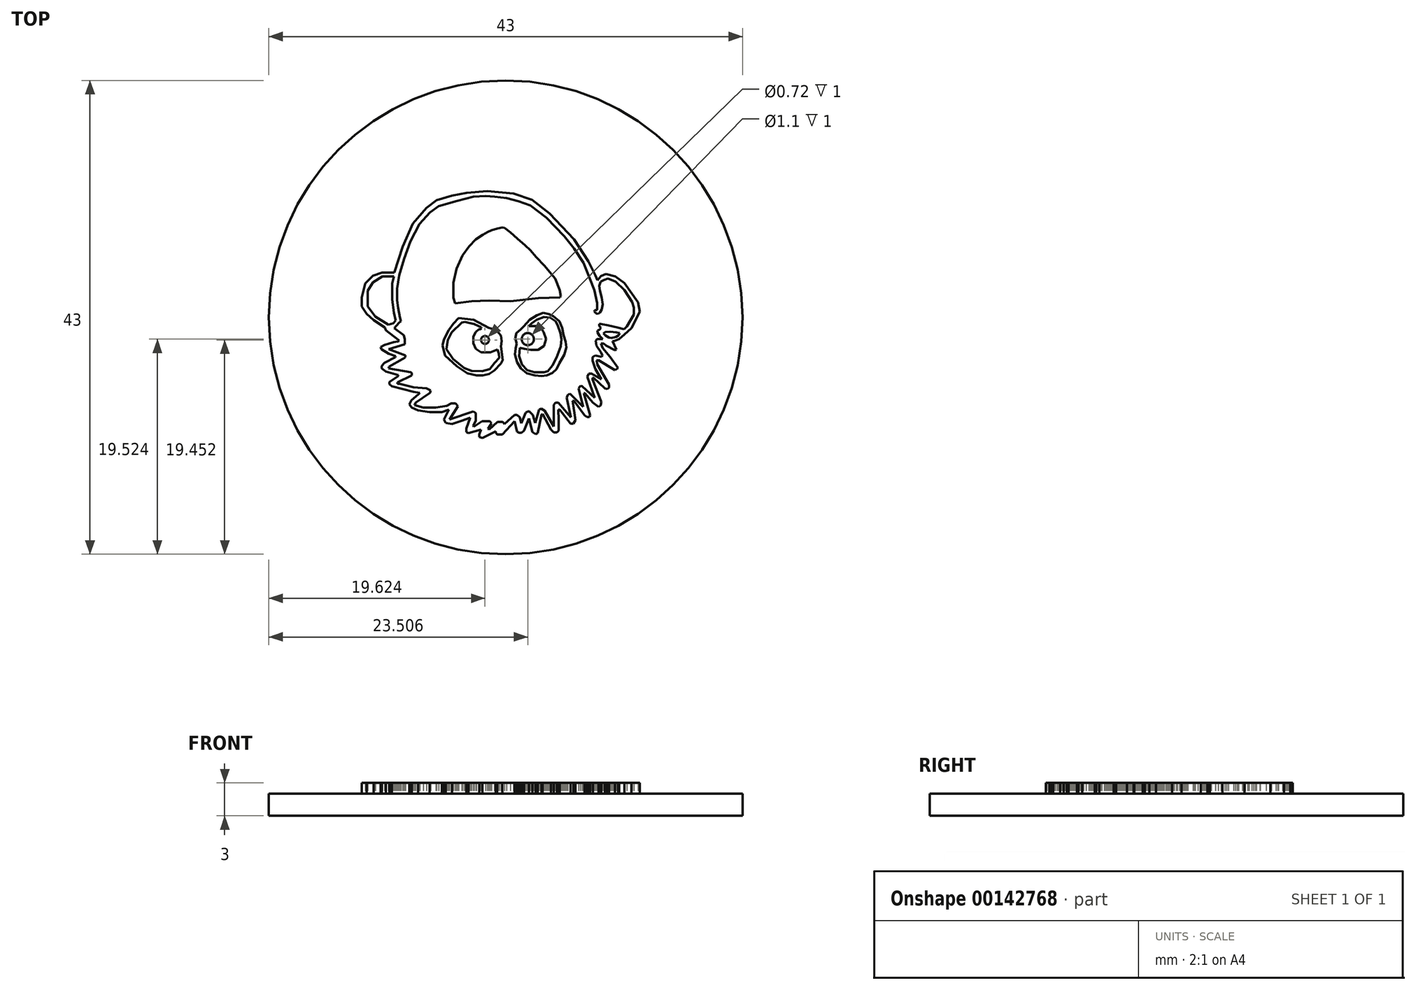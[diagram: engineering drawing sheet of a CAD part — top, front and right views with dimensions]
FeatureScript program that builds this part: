
annotation { "Feature Type Name" : "Feature", "Feature Type Description" : "" }
export const myFeature = defineFeature(function(context is Context, id is Id, definition is map)
    precondition{}
    {
        {
            var Q0;
            Q0=qCreatedBy(makeId("Top.planeOp"),FACE);
            var sketch = newSketch(context, id + "F0", { "sketchPlane" : qUnion([Q0])});
            skLineSegment(sketch, "E0.bottom", {"start": v(22, -30) * mm, "end": v(-22, -30) * mm});
            skLineSegment(sketch, "E0.top", {"start": v(22, 30) * mm, "end": v(-22, 30) * mm});
            skLineSegment(sketch, "E0.left", {"start": v(22, -30) * mm, "end": v(22, 30) * mm});
            skLineSegment(sketch, "E0.right", {"start": v(-22, -30) * mm, "end": v(-22, 30) * mm});
            skPoint(sketch, "E0.middle", {"position": v(0, 0) * mm});
            skCircle(sketch, "E1", {"center": v(0, 0) * mm, "radius": 21.5 * mm, "construction": true});
            skSolve(sketch);
        }
        {
            var Q0;
            Q0=qSketchRegion(id+"F0",true);
            extrude(context, id + "F1", {"entities" : qUnion([Q0]), "oppositeDirection" : true, "depth" : 2 * mm});
        }
        {
            var Q0;
            Q0=makeQuery(id+"F1.opExtrude","CAP_FACE",FACE,{"disambiguationData":[OSD([sQuery(id+"F0.wireOp",EDGE,"E0.bottom"),sQuery(id+"F0.wireOp",EDGE,"E0.top"),sQuery(id+"F0.wireOp",EDGE,"E0.left"),sQuery(id+"F0.wireOp",EDGE,"E0.right")])],"isStart":false});
            var sketch = newSketch(context, id + "F2", { "sketchPlane" : qUnion([Q0])});
            skLineSegment(sketch, "E2", {"start": v(-9.75, 2.02) * mm, "end": v(-10.89, 1.18) * mm});
            skLineSegment(sketch, "E3", {"start": v(-10.89, 1.18) * mm, "end": v(-10.98, 0.9) * mm});
            skLineSegment(sketch, "E4", {"start": v(-10.98, 0.9) * mm, "end": v(-12, 0.26) * mm});
            skLineSegment(sketch, "E5", {"start": v(-12, 0.26) * mm, "end": v(-12.62, -0.33) * mm});
            skLineSegment(sketch, "E6", {"start": v(-12.62, -0.33) * mm, "end": v(-13.05, -0.98) * mm});
            skLineSegment(sketch, "E7", {"start": v(-13.05, -0.98) * mm, "end": v(-13.05, -1.81) * mm});
            skLineSegment(sketch, "E8", {"start": v(-13.05, -1.81) * mm, "end": v(-12.74, -3.08) * mm});
            skLineSegment(sketch, "E9", {"start": v(-12.74, -3.08) * mm, "end": v(-12.06, -3.79) * mm});
            skLineSegment(sketch, "E10", {"start": v(-12.06, -3.79) * mm, "end": v(-11.23, -4.07) * mm});
            skLineSegment(sketch, "E11", {"start": v(-10.12, -4.07) * mm, "end": v(-9.35, -6.41) * mm});
            skLineSegment(sketch, "E12", {"start": v(-9.35, -6.41) * mm, "end": v(-8.42, -8.5) * mm});
            skLineSegment(sketch, "E13", {"start": v(-8.42, -8.5) * mm, "end": v(-7.19, -9.93) * mm});
            skLineSegment(sketch, "E14", {"start": v(-7.19, -9.93) * mm, "end": v(-6.26, -10.64) * mm});
            skLineSegment(sketch, "E15", {"start": v(-6.26, -10.64) * mm, "end": v(-4.87, -11.04) * mm});
            skLineSegment(sketch, "E16", {"start": v(-4.87, -11.04) * mm, "end": v(-3.55, -11.3) * mm});
            skLineSegment(sketch, "E17", {"start": v(-3.55, -11.3) * mm, "end": v(-1.67, -11.47) * mm});
            skLineSegment(sketch, "E18", {"start": v(-1.67, -11.47) * mm, "end": v(0.71, -11.24) * mm});
            skLineSegment(sketch, "E19", {"start": v(0.71, -11.24) * mm, "end": v(2.4, -10.67) * mm});
            skLineSegment(sketch, "E20", {"start": v(2.4, -10.67) * mm, "end": v(3.98, -9.43) * mm});
            skLineSegment(sketch, "E21", {"start": v(3.98, -9.43) * mm, "end": v(6.2, -7.09) * mm});
            skLineSegment(sketch, "E22", {"start": v(6.2, -7.09) * mm, "end": v(7.5, -5.09) * mm});
            skLineSegment(sketch, "E23", {"start": v(7.5, -5.09) * mm, "end": v(8.13, -3.8) * mm});
            skLineSegment(sketch, "E24", {"start": v(8.13, -3.8) * mm, "end": v(8.32, -3.38) * mm});
            skLineSegment(sketch, "E25", {"start": v(8.32, -3.38) * mm, "end": v(8.64, -3.76) * mm});
            skLineSegment(sketch, "E26", {"start": v(8.64, -3.76) * mm, "end": v(9.08, -3.95) * mm});
            skLineSegment(sketch, "E27", {"start": v(9.08, -3.95) * mm, "end": v(9.95, -3.72) * mm});
            skLineSegment(sketch, "E28", {"start": v(9.95, -3.72) * mm, "end": v(10.77, -3.13) * mm});
            skLineSegment(sketch, "E29", {"start": v(10.77, -3.13) * mm, "end": v(12.01, -1.38) * mm});
            skLineSegment(sketch, "E30", {"start": v(12.01, -1.38) * mm, "end": v(12.16, -0.51) * mm});
            skLineSegment(sketch, "E31", {"start": v(12.16, -0.51) * mm, "end": v(11.4, 0.96) * mm});
            skLineSegment(sketch, "E32", {"start": v(11.4, 0.96) * mm, "end": v(10.77, 1.55) * mm});
            skLineSegment(sketch, "E33", {"start": v(10.77, 1.55) * mm, "end": v(10.3, 1.97) * mm});
            skLineSegment(sketch, "E34", {"start": v(10.3, 1.97) * mm, "end": v(9.83, 2.16) * mm});
            skLineSegment(sketch, "E35", {"start": v(9.83, 2.16) * mm, "end": v(9.69, 2.16) * mm});
            skLineSegment(sketch, "E36", {"start": v(9.69, 2.16) * mm, "end": v(10.04, 2.93) * mm});
            skLineSegment(sketch, "E37", {"start": v(10.04, 2.93) * mm, "end": v(9.93, 2.98) * mm});
            skLineSegment(sketch, "E38", {"start": v(9.93, 2.98) * mm, "end": v(9.11, 2.55) * mm});
            skLineSegment(sketch, "E39", {"start": v(9.11, 2.55) * mm, "end": v(8.9, 2.36) * mm});
            skLineSegment(sketch, "E40", {"start": v(8.9, 2.36) * mm, "end": v(8.66, 2.36) * mm});
            skLineSegment(sketch, "E41", {"start": v(8.66, 2.36) * mm, "end": v(8.81, 2.79) * mm});
            skLineSegment(sketch, "E42", {"start": v(8.81, 2.79) * mm, "end": v(9.46, 3.58) * mm});
            skLineSegment(sketch, "E43", {"start": v(9.46, 3.58) * mm, "end": v(10.2, 4.59) * mm});
            skLineSegment(sketch, "E44", {"start": v(10.2, 4.59) * mm, "end": v(9.9, 4.8) * mm});
            skLineSegment(sketch, "E45", {"start": v(9.9, 4.8) * mm, "end": v(8.4, 3.86) * mm});
            skLineSegment(sketch, "E46", {"start": v(8.4, 3.86) * mm, "end": v(8.26, 3.91) * mm});
            skLineSegment(sketch, "E47", {"start": v(8.26, 3.91) * mm, "end": v(8.31, 4.24) * mm});
            skLineSegment(sketch, "E48", {"start": v(8.31, 4.24) * mm, "end": v(9.37, 6.08) * mm});
            skLineSegment(sketch, "E49", {"start": v(9.37, 6.08) * mm, "end": v(9.37, 6.39) * mm});
            skLineSegment(sketch, "E50", {"start": v(9.37, 6.39) * mm, "end": v(9.23, 6.5) * mm});
            skLineSegment(sketch, "E51", {"start": v(9.23, 6.5) * mm, "end": v(9, 6.45) * mm});
            skLineSegment(sketch, "E52", {"start": v(9, 6.45) * mm, "end": v(7.98, 5.49) * mm});
            skLineSegment(sketch, "E53", {"start": v(7.98, 5.49) * mm, "end": v(7.88, 5.49) * mm});
            skLineSegment(sketch, "E54", {"start": v(7.88, 5.49) * mm, "end": v(7.88, 5.64) * mm});
            skLineSegment(sketch, "E55", {"start": v(7.88, 5.64) * mm, "end": v(8.68, 7.66) * mm});
            skLineSegment(sketch, "E56", {"start": v(8.68, 7.66) * mm, "end": v(8.62, 8) * mm});
            skLineSegment(sketch, "E57", {"start": v(8.62, 8) * mm, "end": v(8.43, 8.13) * mm});
            skLineSegment(sketch, "E58", {"start": v(8.43, 8.13) * mm, "end": v(7.93, 7.75) * mm});
            skLineSegment(sketch, "E59", {"start": v(7.93, 7.75) * mm, "end": v(7.2, 6.88) * mm});
            skLineSegment(sketch, "E60", {"start": v(7.2, 6.88) * mm, "end": v(7.1, 6.88) * mm});
            skLineSegment(sketch, "E61", {"start": v(7.1, 6.88) * mm, "end": v(7.67, 8.89) * mm});
            skLineSegment(sketch, "E62", {"start": v(7.67, 8.89) * mm, "end": v(7.6, 9.04) * mm});
            skLineSegment(sketch, "E63", {"start": v(7.6, 9.04) * mm, "end": v(7.4, 9.04) * mm});
            skLineSegment(sketch, "E64", {"start": v(7.4, 9.04) * mm, "end": v(7.17, 8.88) * mm});
            skLineSegment(sketch, "E65", {"start": v(7.17, 8.88) * mm, "end": v(6.2, 7.6) * mm});
            skLineSegment(sketch, "E66", {"start": v(6.2, 7.6) * mm, "end": v(6.09, 7.6) * mm});
            skLineSegment(sketch, "E67", {"start": v(6.09, 7.6) * mm, "end": v(6.32, 9.32) * mm});
            skLineSegment(sketch, "E68", {"start": v(6.32, 9.32) * mm, "end": v(6.15, 9.66) * mm});
            skLineSegment(sketch, "E69", {"start": v(6.15, 9.66) * mm, "end": v(5.9, 9.66) * mm});
            skLineSegment(sketch, "E70", {"start": v(5.9, 9.66) * mm, "end": v(4.9, 8.36) * mm});
            skLineSegment(sketch, "E71", {"start": v(4.9, 8.36) * mm, "end": v(4.77, 8.36) * mm});
            skLineSegment(sketch, "E72", {"start": v(4.77, 8.36) * mm, "end": v(4.82, 9.3) * mm});
            skLineSegment(sketch, "E73", {"start": v(4.82, 9.3) * mm, "end": v(4.82, 10.27) * mm});
            skLineSegment(sketch, "E74", {"start": v(4.82, 10.27) * mm, "end": v(4.64, 10.44) * mm});
            skLineSegment(sketch, "E75", {"start": v(4.64, 10.44) * mm, "end": v(4.36, 10.44) * mm});
            skLineSegment(sketch, "E76", {"start": v(4.36, 10.44) * mm, "end": v(4.12, 10.2) * mm});
            skLineSegment(sketch, "E77", {"start": v(4.12, 10.2) * mm, "end": v(3.35, 8.76) * mm});
            skLineSegment(sketch, "E78", {"start": v(3.35, 8.76) * mm, "end": v(3.26, 8.81) * mm});
            skLineSegment(sketch, "E79", {"start": v(3.26, 8.81) * mm, "end": v(2.92, 10.49) * mm});
            skLineSegment(sketch, "E80", {"start": v(2.92, 10.49) * mm, "end": v(2.7, 10.59) * mm});
            skLineSegment(sketch, "E81", {"start": v(2.7, 10.59) * mm, "end": v(2.45, 10.4) * mm});
            skLineSegment(sketch, "E82", {"start": v(2.45, 10.4) * mm, "end": v(2.11, 9.17) * mm});
            skLineSegment(sketch, "E83", {"start": v(2.11, 9.17) * mm, "end": v(1.67, 10.29) * mm});
            skLineSegment(sketch, "E84", {"start": v(1.67, 10.29) * mm, "end": v(1.44, 10.46) * mm});
            skLineSegment(sketch, "E85", {"start": v(1.44, 10.46) * mm, "end": v(1.21, 10.46) * mm});
            skLineSegment(sketch, "E86", {"start": v(1.21, 10.46) * mm, "end": v(1.03, 10.39) * mm});
            skLineSegment(sketch, "E87", {"start": v(1.03, 10.39) * mm, "end": v(0.83, 9.42) * mm});
            skLineSegment(sketch, "E88", {"start": v(0.83, 9.42) * mm, "end": v(-0.29, 10.62) * mm});
            skLineSegment(sketch, "E89", {"start": v(-0.29, 10.62) * mm, "end": v(-0.76, 10.62) * mm});
            skLineSegment(sketch, "E90", {"start": v(-0.76, 10.62) * mm, "end": v(-0.9, 10.43) * mm});
            skLineSegment(sketch, "E91", {"start": v(-0.9, 10.43) * mm, "end": v(-0.9, 10.35) * mm});
            skLineSegment(sketch, "E92", {"start": v(-0.9, 10.35) * mm, "end": v(-2.1, 10.95) * mm});
            skLineSegment(sketch, "E93", {"start": v(-2.1, 10.95) * mm, "end": v(-2.39, 10.85) * mm});
            skLineSegment(sketch, "E94", {"start": v(-2.39, 10.85) * mm, "end": v(-2.39, 10.63) * mm});
            skLineSegment(sketch, "E95", {"start": v(-2.39, 10.63) * mm, "end": v(-2.24, 10.17) * mm});
            skLineSegment(sketch, "E96", {"start": v(-2.24, 10.17) * mm, "end": v(-3.37, 10.52) * mm});
            skLineSegment(sketch, "E97", {"start": v(-3.37, 10.52) * mm, "end": v(-3.56, 10.4) * mm});
            skLineSegment(sketch, "E98", {"start": v(-3.56, 10.4) * mm, "end": v(-3.56, 10.09) * mm});
            skLineSegment(sketch, "E99", {"start": v(-3.56, 10.09) * mm, "end": v(-3.2, 9.1) * mm});
            skLineSegment(sketch, "E100", {"start": v(-3.2, 9.1) * mm, "end": v(-4, 9.38) * mm});
            skLineSegment(sketch, "E101", {"start": v(-4, 9.38) * mm, "end": v(-4.87, 9.67) * mm});
            skLineSegment(sketch, "E102", {"start": v(-4.87, 9.67) * mm, "end": v(-5.43, 9.58) * mm});
            skLineSegment(sketch, "E103", {"start": v(-5.43, 9.58) * mm, "end": v(-5.6, 9.28) * mm});
            skLineSegment(sketch, "E104", {"start": v(-5.6, 9.28) * mm, "end": v(-5.17, 8.38) * mm});
            skLineSegment(sketch, "E105", {"start": v(-5.17, 8.38) * mm, "end": v(-5.8, 8.61) * mm});
            skLineSegment(sketch, "E106", {"start": v(-5.8, 8.61) * mm, "end": v(-6.91, 8.61) * mm});
            skLineSegment(sketch, "E107", {"start": v(-6.91, 8.61) * mm, "end": v(-7.95, 8.44) * mm});
            skLineSegment(sketch, "E108", {"start": v(-7.95, 8.44) * mm, "end": v(-8.52, 8.18) * mm});
            skLineSegment(sketch, "E109", {"start": v(-8.52, 8.18) * mm, "end": v(-8.74, 7.9) * mm});
            skLineSegment(sketch, "E110", {"start": v(-8.74, 7.9) * mm, "end": v(-8.57, 7.53) * mm});
            skLineSegment(sketch, "E111", {"start": v(-8.57, 7.53) * mm, "end": v(-7.93, 7) * mm});
            skLineSegment(sketch, "E112", {"start": v(-7.93, 7) * mm, "end": v(-7.8, 6.85) * mm});
            skLineSegment(sketch, "E113", {"start": v(-7.8, 6.85) * mm, "end": v(-8.38, 6.75) * mm});
            skLineSegment(sketch, "E114", {"start": v(-8.38, 6.75) * mm, "end": v(-10.34, 6.26) * mm});
            skLineSegment(sketch, "E115", {"start": v(-10.34, 6.26) * mm, "end": v(-10.55, 6.05) * mm});
            skLineSegment(sketch, "E116", {"start": v(-10.55, 6.05) * mm, "end": v(-10.55, 5.86) * mm});
            skLineSegment(sketch, "E117", {"start": v(-10.55, 5.86) * mm, "end": v(-9.76, 5.34) * mm});
            skLineSegment(sketch, "E118", {"start": v(-9.76, 5.34) * mm, "end": v(-9.76, 5.23) * mm});
            skLineSegment(sketch, "E119", {"start": v(-9.76, 5.23) * mm, "end": v(-10.86, 4.9) * mm});
            skLineSegment(sketch, "E120", {"start": v(-10.86, 4.9) * mm, "end": v(-11.24, 4.64) * mm});
            skLineSegment(sketch, "E121", {"start": v(-11.24, 4.64) * mm, "end": v(-11.24, 4.41) * mm});
            skLineSegment(sketch, "E122", {"start": v(-11.24, 4.41) * mm, "end": v(-11, 4.13) * mm});
            skLineSegment(sketch, "E123", {"start": v(-11, 4.13) * mm, "end": v(-10.03, 3.62) * mm});
            skLineSegment(sketch, "E124", {"start": v(-10.03, 3.62) * mm, "end": v(-10, 3.53) * mm});
            skLineSegment(sketch, "E125", {"start": v(-10, 3.53) * mm, "end": v(-10.62, 3.3) * mm});
            skLineSegment(sketch, "E126", {"start": v(-10.62, 3.3) * mm, "end": v(-11.28, 2.88) * mm});
            skLineSegment(sketch, "E127", {"start": v(-11.28, 2.88) * mm, "end": v(-11.37, 2.7) * mm});
            skLineSegment(sketch, "E128", {"start": v(-11.37, 2.7) * mm, "end": v(-10.99, 2.52) * mm});
            skLineSegment(sketch, "E129", {"start": v(-10.99, 2.52) * mm, "end": v(-10.19, 2.25) * mm});
            skLineSegment(sketch, "E130", {"start": v(-10.19, 2.25) * mm, "end": v(-9.8, 2.17) * mm});
            skLineSegment(sketch, "E131", {"start": v(-9.8, 2.17) * mm, "end": v(-9.68, 2.13) * mm});
            skLineSegment(sketch, "E132", {"start": v(-9.68, 2.13) * mm, "end": v(-9.75, 2.02) * mm});
            skLineSegment(sketch, "E133", {"start": v(-10.66, 0.67) * mm, "end": v(-11.83, -0.05) * mm});
            skLineSegment(sketch, "E134", {"start": v(-11.83, -0.05) * mm, "end": v(-12.51, -0.98) * mm});
            skLineSegment(sketch, "E135", {"start": v(-12.51, -0.98) * mm, "end": v(-12.51, -2.42) * mm});
            skLineSegment(sketch, "E136", {"start": v(-12.51, -2.42) * mm, "end": v(-12.05, -3.19) * mm});
            skLineSegment(sketch, "E137", {"start": v(-12.05, -3.19) * mm, "end": v(-11.2, -3.73) * mm});
            skLineSegment(sketch, "E138", {"start": v(-11.2, -3.73) * mm, "end": v(-10.15, -3.73) * mm});
            skLineSegment(sketch, "E139", {"start": v(-10.15, -3.73) * mm, "end": v(-10.31, -3.08) * mm});
            skLineSegment(sketch, "E140", {"start": v(-10.31, -3.08) * mm, "end": v(-10.31, -1.61) * mm});
            skLineSegment(sketch, "E141", {"start": v(-10.31, -1.61) * mm, "end": v(-10.14, -0.41) * mm});
            skLineSegment(sketch, "E142", {"start": v(-10.14, -0.41) * mm, "end": v(-9.97, 0.28) * mm});
            skLineSegment(sketch, "E143", {"start": v(-9.97, 0.28) * mm, "end": v(-10.21, 0.54) * mm});
            skLineSegment(sketch, "E144", {"start": v(-10.21, 0.54) * mm, "end": v(-10.66, 0.67) * mm});
            skLineSegment(sketch, "E145", {"start": v(-4.6, -1.26) * mm, "end": v(-3.08, -1.46) * mm});
            skLineSegment(sketch, "E146", {"start": v(-3.08, -1.46) * mm, "end": v(-1.52, -1.53) * mm});
            skLineSegment(sketch, "E147", {"start": v(-1.52, -1.53) * mm, "end": v(0.42, -1.48) * mm});
            skLineSegment(sketch, "E148", {"start": v(0.42, -1.48) * mm, "end": v(2.98, -1.76) * mm});
            skLineSegment(sketch, "E149", {"start": v(2.98, -1.76) * mm, "end": v(4.93, -1.82) * mm});
            skLineSegment(sketch, "E150", {"start": v(4.93, -1.82) * mm, "end": v(5, -1.95) * mm});
            skLineSegment(sketch, "E151", {"start": v(5, -1.95) * mm, "end": v(4.9, -2.48) * mm});
            skLineSegment(sketch, "E152", {"start": v(4.9, -2.48) * mm, "end": v(4.5, -3.53) * mm});
            skLineSegment(sketch, "E153", {"start": v(4.5, -3.53) * mm, "end": v(3.5, -4.7) * mm});
            skLineSegment(sketch, "E154", {"start": v(3.5, -4.7) * mm, "end": v(2.8, -5.47) * mm});
            skLineSegment(sketch, "E155", {"start": v(2.8, -5.47) * mm, "end": v(2.24, -6.1) * mm});
            skLineSegment(sketch, "E156", {"start": v(2.24, -6.1) * mm, "end": v(1.76, -6.53) * mm});
            skLineSegment(sketch, "E157", {"start": v(1.76, -6.53) * mm, "end": v(1.07, -7.14) * mm});
            skLineSegment(sketch, "E158", {"start": v(1.07, -7.14) * mm, "end": v(0.44, -7.73) * mm});
            skLineSegment(sketch, "E159", {"start": v(0.44, -7.73) * mm, "end": v(-0.1, -8.13) * mm});
            skLineSegment(sketch, "E160", {"start": v(-0.1, -8.13) * mm, "end": v(-0.32, -8.17) * mm});
            skLineSegment(sketch, "E161", {"start": v(-0.32, -8.17) * mm, "end": v(-0.75, -8.06) * mm});
            skLineSegment(sketch, "E162", {"start": v(-0.75, -8.06) * mm, "end": v(-1.27, -7.9) * mm});
            skLineSegment(sketch, "E163", {"start": v(-1.27, -7.9) * mm, "end": v(-1.63, -7.76) * mm});
            skLineSegment(sketch, "E164", {"start": v(-1.63, -7.76) * mm, "end": v(-2.09, -7.49) * mm});
            skLineSegment(sketch, "E165", {"start": v(-2.09, -7.49) * mm, "end": v(-2.7, -7.08) * mm});
            skLineSegment(sketch, "E166", {"start": v(-2.7, -7.08) * mm, "end": v(-3.32, -6.46) * mm});
            skLineSegment(sketch, "E167", {"start": v(-3.32, -6.46) * mm, "end": v(-3.9, -5.62) * mm});
            skLineSegment(sketch, "E168", {"start": v(-3.9, -5.62) * mm, "end": v(-4.45, -4.43) * mm});
            skLineSegment(sketch, "E169", {"start": v(-4.45, -4.43) * mm, "end": v(-4.74, -3.15) * mm});
            skLineSegment(sketch, "E170", {"start": v(-4.74, -3.15) * mm, "end": v(-4.74, -1.77) * mm});
            skLineSegment(sketch, "E171", {"start": v(-4.74, -1.77) * mm, "end": v(-4.6, -1.26) * mm});
            skLineSegment(sketch, "E172", {"start": v(-10.12, 0.98) * mm, "end": v(-9.7, 0.5) * mm});
            skLineSegment(sketch, "E173", {"start": v(-9.7, 0.5) * mm, "end": v(-9.52, 0.33) * mm});
            skLineSegment(sketch, "E174", {"start": v(-9.52, 0.33) * mm, "end": v(-9.61, -0.02) * mm});
            skLineSegment(sketch, "E175", {"start": v(-9.61, -0.02) * mm, "end": v(-9.75, -0.87) * mm});
            skLineSegment(sketch, "E176", {"start": v(-9.75, -0.87) * mm, "end": v(-9.86, -1.57) * mm});
            skLineSegment(sketch, "E177", {"start": v(-9.86, -1.57) * mm, "end": v(-9.86, -2.6) * mm});
            skLineSegment(sketch, "E178", {"start": v(-9.86, -2.6) * mm, "end": v(-9.66, -3.8) * mm});
            skLineSegment(sketch, "E179", {"start": v(-9.66, -3.8) * mm, "end": v(-9.22, -5.3) * mm});
            skLineSegment(sketch, "E180", {"start": v(-9.22, -5.3) * mm, "end": v(-8.65, -6.88) * mm});
            skLineSegment(sketch, "E181", {"start": v(-8.65, -6.88) * mm, "end": v(-7.82, -8.48) * mm});
            skLineSegment(sketch, "E182", {"start": v(-7.82, -8.48) * mm, "end": v(-6.89, -9.52) * mm});
            skLineSegment(sketch, "E183", {"start": v(-6.89, -9.52) * mm, "end": v(-6.08, -10.1) * mm});
            skLineSegment(sketch, "E184", {"start": v(-6.08, -10.1) * mm, "end": v(-4.4, -10.57) * mm});
            skLineSegment(sketch, "E185", {"start": v(-4.4, -10.57) * mm, "end": v(-2.93, -10.95) * mm});
            skLineSegment(sketch, "E186", {"start": v(-2.93, -10.95) * mm, "end": v(-1.83, -11) * mm});
            skLineSegment(sketch, "E187", {"start": v(-1.83, -11) * mm, "end": v(-1, -10.95) * mm});
            skLineSegment(sketch, "E188", {"start": v(-1, -10.95) * mm, "end": v(0.09, -10.82) * mm});
            skLineSegment(sketch, "E189", {"start": v(0.09, -10.82) * mm, "end": v(1.16, -10.54) * mm});
            skLineSegment(sketch, "E190", {"start": v(1.16, -10.54) * mm, "end": v(2.23, -10.17) * mm});
            skLineSegment(sketch, "E191", {"start": v(2.23, -10.17) * mm, "end": v(3.7, -9.05) * mm});
            skLineSegment(sketch, "E192", {"start": v(3.7, -9.05) * mm, "end": v(5.31, -7.37) * mm});
            skLineSegment(sketch, "E193", {"start": v(5.31, -7.37) * mm, "end": v(6.2, -6.25) * mm});
            skLineSegment(sketch, "E194", {"start": v(6.2, -6.25) * mm, "end": v(7.08, -4.96) * mm});
            skLineSegment(sketch, "E195", {"start": v(7.08, -4.96) * mm, "end": v(7.63, -3.54) * mm});
            skLineSegment(sketch, "E196", {"start": v(7.63, -3.54) * mm, "end": v(8.05, -2.5) * mm});
            skLineSegment(sketch, "E197", {"start": v(8.05, -2.5) * mm, "end": v(8.3, -1.31) * mm});
            skLineSegment(sketch, "E198", {"start": v(8.3, -1.31) * mm, "end": v(8.3, -0.66) * mm});
            skLineSegment(sketch, "E199", {"start": v(8.3, -0.66) * mm, "end": v(8.2, -0.66) * mm});
            skLineSegment(sketch, "E200", {"start": v(8.2, -0.66) * mm, "end": v(8.07, -0.64) * mm});
            skLineSegment(sketch, "E201", {"start": v(8.07, -0.64) * mm, "end": v(8.06, -0.52) * mm});
            skLineSegment(sketch, "E202", {"start": v(8.06, -0.52) * mm, "end": v(8.25, -0.34) * mm});
            skLineSegment(sketch, "E203", {"start": v(8.25, -0.34) * mm, "end": v(8.4, -0.32) * mm});
            skLineSegment(sketch, "E204", {"start": v(8.4, -0.32) * mm, "end": v(8.56, -0.45) * mm});
            skLineSegment(sketch, "E205", {"start": v(8.56, -0.45) * mm, "end": v(8.73, -0.72) * mm});
            skLineSegment(sketch, "E206", {"start": v(8.73, -0.72) * mm, "end": v(8.8, -1.18) * mm});
            skLineSegment(sketch, "E207", {"start": v(8.8, -1.18) * mm, "end": v(8.71, -1.81) * mm});
            skLineSegment(sketch, "E208", {"start": v(8.71, -1.81) * mm, "end": v(8.56, -2.43) * mm});
            skLineSegment(sketch, "E209", {"start": v(8.56, -2.43) * mm, "end": v(8.48, -2.85) * mm});
            skLineSegment(sketch, "E210", {"start": v(8.48, -2.85) * mm, "end": v(8.61, -3.24) * mm});
            skLineSegment(sketch, "E211", {"start": v(8.61, -3.24) * mm, "end": v(8.93, -3.42) * mm});
            skLineSegment(sketch, "E212", {"start": v(8.93, -3.42) * mm, "end": v(9.28, -3.54) * mm});
            skLineSegment(sketch, "E213", {"start": v(9.28, -3.54) * mm, "end": v(9.97, -3.23) * mm});
            skLineSegment(sketch, "E214", {"start": v(9.97, -3.23) * mm, "end": v(10.78, -2.48) * mm});
            skLineSegment(sketch, "E215", {"start": v(10.78, -2.48) * mm, "end": v(11.47, -1.4) * mm});
            skLineSegment(sketch, "E216", {"start": v(11.47, -1.4) * mm, "end": v(11.62, -0.9) * mm});
            skLineSegment(sketch, "E217", {"start": v(11.62, -0.9) * mm, "end": v(11.62, -0.25) * mm});
            skLineSegment(sketch, "E218", {"start": v(11.62, -0.25) * mm, "end": v(11, 0.83) * mm});
            skLineSegment(sketch, "E219", {"start": v(11, 0.83) * mm, "end": v(10.74, 1.08) * mm});
            skLineSegment(sketch, "E220", {"start": v(10.74, 1.08) * mm, "end": v(10.13, 0.92) * mm});
            skLineSegment(sketch, "E221", {"start": v(10.13, 0.92) * mm, "end": v(9.31, 0.72) * mm});
            skLineSegment(sketch, "E222", {"start": v(9.31, 0.72) * mm, "end": v(8.65, 0.6) * mm});
            skLineSegment(sketch, "E223", {"start": v(8.65, 0.6) * mm, "end": v(8.5, 0.59) * mm});
            skLineSegment(sketch, "E224", {"start": v(8.5, 0.59) * mm, "end": v(8.5, 0.8) * mm});
            skLineSegment(sketch, "E225", {"start": v(8.5, 0.8) * mm, "end": v(8.67, 0.95) * mm});
            skLineSegment(sketch, "E226", {"start": v(8.67, 0.95) * mm, "end": v(8.52, 1.12) * mm});
            skLineSegment(sketch, "E227", {"start": v(8.52, 1.12) * mm, "end": v(8.34, 1.19) * mm});
            skLineSegment(sketch, "E228", {"start": v(8.34, 1.19) * mm, "end": v(8.34, 1.37) * mm});
            skLineSegment(sketch, "E229", {"start": v(8.34, 1.37) * mm, "end": v(8.51, 1.69) * mm});
            skLineSegment(sketch, "E230", {"start": v(8.51, 1.69) * mm, "end": v(8.81, 1.96) * mm});
            skLineSegment(sketch, "E231", {"start": v(8.81, 1.96) * mm, "end": v(8.32, 1.96) * mm});
            skLineSegment(sketch, "E232", {"start": v(8.32, 1.96) * mm, "end": v(8.17, 2.12) * mm});
            skLineSegment(sketch, "E233", {"start": v(8.17, 2.12) * mm, "end": v(8.25, 2.55) * mm});
            skLineSegment(sketch, "E234", {"start": v(8.25, 2.55) * mm, "end": v(8.65, 3.17) * mm});
            skLineSegment(sketch, "E235", {"start": v(8.65, 3.17) * mm, "end": v(8.78, 3.45) * mm});
            skLineSegment(sketch, "E236", {"start": v(8.78, 3.45) * mm, "end": v(8.7, 3.59) * mm});
            skLineSegment(sketch, "E237", {"start": v(8.7, 3.59) * mm, "end": v(8.1, 3.45) * mm});
            skLineSegment(sketch, "E238", {"start": v(8.1, 3.45) * mm, "end": v(7.89, 3.6) * mm});
            skLineSegment(sketch, "E239", {"start": v(7.89, 3.6) * mm, "end": v(7.89, 3.95) * mm});
            skLineSegment(sketch, "E240", {"start": v(7.89, 3.95) * mm, "end": v(8.15, 4.68) * mm});
            skLineSegment(sketch, "E241", {"start": v(8.15, 4.68) * mm, "end": v(8.7, 5.63) * mm});
            skLineSegment(sketch, "E242", {"start": v(8.7, 5.63) * mm, "end": v(7.8, 5.1) * mm});
            skLineSegment(sketch, "E243", {"start": v(7.8, 5.1) * mm, "end": v(7.54, 5.1) * mm});
            skLineSegment(sketch, "E244", {"start": v(7.54, 5.1) * mm, "end": v(7.4, 5.38) * mm});
            skLineSegment(sketch, "E245", {"start": v(7.4, 5.38) * mm, "end": v(8.07, 7.3) * mm});
            skLineSegment(sketch, "E246", {"start": v(8.07, 7.3) * mm, "end": v(6.94, 6.25) * mm});
            skLineSegment(sketch, "E247", {"start": v(6.94, 6.25) * mm, "end": v(6.77, 6.23) * mm});
            skLineSegment(sketch, "E248", {"start": v(6.77, 6.23) * mm, "end": v(6.63, 6.43) * mm});
            skLineSegment(sketch, "E249", {"start": v(6.63, 6.43) * mm, "end": v(7.03, 8.1) * mm});
            skLineSegment(sketch, "E250", {"start": v(7.03, 8.1) * mm, "end": v(5.81, 6.93) * mm});
            skLineSegment(sketch, "E251", {"start": v(5.81, 6.93) * mm, "end": v(5.64, 7.04) * mm});
            skLineSegment(sketch, "E252", {"start": v(5.64, 7.04) * mm, "end": v(5.54, 7.3) * mm});
            skLineSegment(sketch, "E253", {"start": v(5.54, 7.3) * mm, "end": v(5.9, 9.06) * mm});
            skLineSegment(sketch, "E254", {"start": v(5.9, 9.06) * mm, "end": v(4.77, 7.73) * mm});
            skLineSegment(sketch, "E255", {"start": v(4.77, 7.73) * mm, "end": v(4.52, 7.73) * mm});
            skLineSegment(sketch, "E256", {"start": v(4.52, 7.73) * mm, "end": v(4.36, 7.94) * mm});
            skLineSegment(sketch, "E257", {"start": v(4.36, 7.94) * mm, "end": v(4.36, 9.91) * mm});
            skLineSegment(sketch, "E258", {"start": v(4.36, 9.91) * mm, "end": v(3.55, 8.47) * mm});
            skLineSegment(sketch, "E259", {"start": v(3.55, 8.47) * mm, "end": v(3.24, 8.28) * mm});
            skLineSegment(sketch, "E260", {"start": v(3.24, 8.28) * mm, "end": v(3.04, 8.37) * mm});
            skLineSegment(sketch, "E261", {"start": v(3.04, 8.37) * mm, "end": v(2.7, 9.58) * mm});
            skLineSegment(sketch, "E262", {"start": v(2.7, 9.58) * mm, "end": v(2.47, 8.86) * mm});
            skLineSegment(sketch, "E263", {"start": v(2.47, 8.86) * mm, "end": v(2.11, 8.5) * mm});
            skLineSegment(sketch, "E264", {"start": v(2.11, 8.5) * mm, "end": v(1.82, 8.62) * mm});
            skLineSegment(sketch, "E265", {"start": v(1.82, 8.62) * mm, "end": v(1.4, 9.61) * mm});
            skLineSegment(sketch, "E266", {"start": v(1.4, 9.61) * mm, "end": v(1.28, 9.09) * mm});
            skLineSegment(sketch, "E267", {"start": v(1.28, 9.09) * mm, "end": v(1.03, 8.86) * mm});
            skLineSegment(sketch, "E268", {"start": v(1.03, 8.86) * mm, "end": v(0.82, 8.86) * mm});
            skLineSegment(sketch, "E269", {"start": v(0.82, 8.86) * mm, "end": v(-0.1, 9.68) * mm});
            skLineSegment(sketch, "E270", {"start": v(-0.1, 9.68) * mm, "end": v(-0.28, 9.48) * mm});
            skLineSegment(sketch, "E271", {"start": v(-0.28, 9.48) * mm, "end": v(-0.75, 9.48) * mm});
            skLineSegment(sketch, "E272", {"start": v(-0.75, 9.48) * mm, "end": v(-1.51, 10.2) * mm});
            skLineSegment(sketch, "E273", {"start": v(-1.51, 10.2) * mm, "end": v(-1.6, 10.1) * mm});
            skLineSegment(sketch, "E274", {"start": v(-1.6, 10.1) * mm, "end": v(-1.3, 9.62) * mm});
            skLineSegment(sketch, "E275", {"start": v(-1.3, 9.62) * mm, "end": v(-1.44, 9.43) * mm});
            skLineSegment(sketch, "E276", {"start": v(-1.44, 9.43) * mm, "end": v(-2.14, 9.43) * mm});
            skLineSegment(sketch, "E277", {"start": v(-2.14, 9.43) * mm, "end": v(-2.9, 9.94) * mm});
            skLineSegment(sketch, "E278", {"start": v(-2.9, 9.94) * mm, "end": v(-2.95, 9.85) * mm});
            skLineSegment(sketch, "E279", {"start": v(-2.95, 9.85) * mm, "end": v(-2.7, 9.38) * mm});
            skLineSegment(sketch, "E280", {"start": v(-2.7, 9.38) * mm, "end": v(-2.7, 8.7) * mm});
            skLineSegment(sketch, "E281", {"start": v(-2.7, 8.7) * mm, "end": v(-2.95, 8.52) * mm});
            skLineSegment(sketch, "E282", {"start": v(-2.95, 8.52) * mm, "end": v(-5.1, 9.26) * mm});
            skLineSegment(sketch, "E283", {"start": v(-5.1, 9.26) * mm, "end": v(-4.34, 8.07) * mm});
            skLineSegment(sketch, "E284", {"start": v(-4.34, 8.07) * mm, "end": v(-4.56, 7.8) * mm});
            skLineSegment(sketch, "E285", {"start": v(-4.56, 7.8) * mm, "end": v(-4.94, 7.8) * mm});
            skLineSegment(sketch, "E286", {"start": v(-4.94, 7.8) * mm, "end": v(-5.36, 8.02) * mm});
            skLineSegment(sketch, "E287", {"start": v(-5.36, 8.02) * mm, "end": v(-6.35, 8.2) * mm});
            skLineSegment(sketch, "E288", {"start": v(-6.35, 8.2) * mm, "end": v(-7.48, 8.2) * mm});
            skLineSegment(sketch, "E289", {"start": v(-7.48, 8.2) * mm, "end": v(-8.26, 7.96) * mm});
            skLineSegment(sketch, "E290", {"start": v(-8.26, 7.96) * mm, "end": v(-8.16, 7.75) * mm});
            skLineSegment(sketch, "E291", {"start": v(-8.16, 7.75) * mm, "end": v(-6.86, 6.86) * mm});
            skLineSegment(sketch, "E292", {"start": v(-6.86, 6.86) * mm, "end": v(-6.81, 6.65) * mm});
            skLineSegment(sketch, "E293", {"start": v(-6.81, 6.65) * mm, "end": v(-7.18, 6.44) * mm});
            skLineSegment(sketch, "E294", {"start": v(-7.18, 6.44) * mm, "end": v(-8.35, 6.36) * mm});
            skLineSegment(sketch, "E295", {"start": v(-8.35, 6.36) * mm, "end": v(-9.65, 6.02) * mm});
            skLineSegment(sketch, "E296", {"start": v(-9.65, 6.02) * mm, "end": v(-9.82, 6.02) * mm});
            skLineSegment(sketch, "E297", {"start": v(-9.82, 6.02) * mm, "end": v(-9.82, 5.9) * mm});
            skLineSegment(sketch, "E298", {"start": v(-9.82, 5.9) * mm, "end": v(-8.52, 5.26) * mm});
            skLineSegment(sketch, "E299", {"start": v(-8.52, 5.26) * mm, "end": v(-8.52, 5.05) * mm});
            skLineSegment(sketch, "E300", {"start": v(-8.52, 5.05) * mm, "end": v(-8.62, 4.97) * mm});
            skLineSegment(sketch, "E301", {"start": v(-8.62, 4.97) * mm, "end": v(-10.62, 4.64) * mm});
            skLineSegment(sketch, "E302", {"start": v(-10.62, 4.64) * mm, "end": v(-10.6, 4.46) * mm});
            skLineSegment(sketch, "E303", {"start": v(-10.6, 4.46) * mm, "end": v(-9.35, 3.78) * mm});
            skLineSegment(sketch, "E304", {"start": v(-9.35, 3.78) * mm, "end": v(-9.12, 3.65) * mm});
            skLineSegment(sketch, "E305", {"start": v(-9.12, 3.65) * mm, "end": v(-9.09, 3.44) * mm});
            skLineSegment(sketch, "E306", {"start": v(-9.09, 3.44) * mm, "end": v(-10.63, 2.87) * mm});
            skLineSegment(sketch, "E307", {"start": v(-10.63, 2.87) * mm, "end": v(-9.15, 2.44) * mm});
            skLineSegment(sketch, "E308", {"start": v(-9.15, 2.44) * mm, "end": v(-9.15, 1.97) * mm});
            skLineSegment(sketch, "E309", {"start": v(-9.15, 1.97) * mm, "end": v(-9.26, 1.63) * mm});
            skLineSegment(sketch, "E310", {"start": v(-9.26, 1.63) * mm, "end": v(-10.12, 0.98) * mm});
            skLineSegment(sketch, "E311", {"start": v(-3.49, 5.08) * mm, "end": v(-4.44, 4.42) * mm});
            skLineSegment(sketch, "E312", {"start": v(-4.44, 4.42) * mm, "end": v(-5.5, 3.46) * mm});
            skLineSegment(sketch, "E313", {"start": v(-5.5, 3.46) * mm, "end": v(-5.72, 2.55) * mm});
            skLineSegment(sketch, "E314", {"start": v(-5.72, 2.55) * mm, "end": v(-5.6, 2) * mm});
            skLineSegment(sketch, "E315", {"start": v(-5.6, 2) * mm, "end": v(-5.17, 1.14) * mm});
            skLineSegment(sketch, "E316", {"start": v(-5.17, 1.14) * mm, "end": v(-4.75, 0.56) * mm});
            skLineSegment(sketch, "E317", {"start": v(-4.75, 0.56) * mm, "end": v(-4.26, 0.07) * mm});
            skLineSegment(sketch, "E318", {"start": v(-4.26, 0.07) * mm, "end": v(-2.89, 0.23) * mm});
            skLineSegment(sketch, "E319", {"start": v(-2.89, 0.23) * mm, "end": v(-1.52, 0.95) * mm});
            skLineSegment(sketch, "E320", {"start": v(-1.52, 0.95) * mm, "end": v(-0.87, 1.12) * mm});
            skLineSegment(sketch, "E321", {"start": v(-0.87, 1.12) * mm, "end": v(-0.44, 1.64) * mm});
            skLineSegment(sketch, "E322", {"start": v(-0.44, 1.64) * mm, "end": v(-0.36, 2.15) * mm});
            skLineSegment(sketch, "E323", {"start": v(-0.36, 2.15) * mm, "end": v(-0.42, 2.65) * mm});
            skLineSegment(sketch, "E324", {"start": v(-0.42, 2.65) * mm, "end": v(-0.25, 3.87) * mm});
            skLineSegment(sketch, "E325", {"start": v(-0.25, 3.87) * mm, "end": v(-0.42, 4.18) * mm});
            skLineSegment(sketch, "E326", {"start": v(-0.42, 4.18) * mm, "end": v(-1.03, 4.83) * mm});
            skLineSegment(sketch, "E327", {"start": v(-1.03, 4.83) * mm, "end": v(-1.5, 5.15) * mm});
            skLineSegment(sketch, "E328", {"start": v(-1.5, 5.15) * mm, "end": v(-2.07, 5.26) * mm});
            skLineSegment(sketch, "E329", {"start": v(-2.07, 5.26) * mm, "end": v(-2.66, 5.26) * mm});
            skLineSegment(sketch, "E330", {"start": v(-2.66, 5.26) * mm, "end": v(-3.49, 5.08) * mm});
            skLineSegment(sketch, "E331", {"start": v(-0.75, 2.92) * mm, "end": v(-1.39, 3.17) * mm});
            skLineSegment(sketch, "E332", {"start": v(-1.39, 3.17) * mm, "end": v(-2.22, 3.18) * mm});
            skLineSegment(sketch, "E333", {"start": v(-2.22, 3.18) * mm, "end": v(-2.7, 2.85) * mm});
            skLineSegment(sketch, "E334", {"start": v(-2.7, 2.85) * mm, "end": v(-2.92, 2.36) * mm});
            skLineSegment(sketch, "E335", {"start": v(-2.92, 2.36) * mm, "end": v(-2.92, 1.75) * mm});
            skLineSegment(sketch, "E336", {"start": v(-2.92, 1.75) * mm, "end": v(-2.71, 1.32) * mm});
            skLineSegment(sketch, "E337", {"start": v(-2.71, 1.32) * mm, "end": v(-2.43, 1.08) * mm});
            skLineSegment(sketch, "E338", {"start": v(-2.43, 1.08) * mm, "end": v(-2.26, 1.07) * mm});
            skLineSegment(sketch, "E339", {"start": v(-2.26, 1.07) * mm, "end": v(-2.2, 1) * mm});
            skLineSegment(sketch, "E340", {"start": v(-2.2, 1) * mm, "end": v(-2.24, 0.89) * mm});
            skLineSegment(sketch, "E341", {"start": v(-2.24, 0.89) * mm, "end": v(-2.47, 0.77) * mm});
            skLineSegment(sketch, "E342", {"start": v(-2.47, 0.77) * mm, "end": v(-2.88, 0.59) * mm});
            skLineSegment(sketch, "E343", {"start": v(-2.88, 0.59) * mm, "end": v(-3.32, 0.5) * mm});
            skLineSegment(sketch, "E344", {"start": v(-3.32, 0.5) * mm, "end": v(-3.68, 0.42) * mm});
            skLineSegment(sketch, "E345", {"start": v(-3.68, 0.42) * mm, "end": v(-4, 0.46) * mm});
            skLineSegment(sketch, "E346", {"start": v(-4, 0.46) * mm, "end": v(-4.9, 1.37) * mm});
            skLineSegment(sketch, "E347", {"start": v(-4.9, 1.37) * mm, "end": v(-5.26, 2.06) * mm});
            skLineSegment(sketch, "E348", {"start": v(-5.26, 2.06) * mm, "end": v(-5.4, 2.9) * mm});
            skLineSegment(sketch, "E349", {"start": v(-5.4, 2.9) * mm, "end": v(-4.79, 3.79) * mm});
            skLineSegment(sketch, "E350", {"start": v(-4.79, 3.79) * mm, "end": v(-3.78, 4.59) * mm});
            skLineSegment(sketch, "E351", {"start": v(-3.78, 4.59) * mm, "end": v(-3.1, 4.86) * mm});
            skLineSegment(sketch, "E352", {"start": v(-3.1, 4.86) * mm, "end": v(-2.15, 4.88) * mm});
            skLineSegment(sketch, "E353", {"start": v(-2.15, 4.88) * mm, "end": v(-1.44, 4.7) * mm});
            skLineSegment(sketch, "E354", {"start": v(-1.44, 4.7) * mm, "end": v(-1, 4.14) * mm});
            skLineSegment(sketch, "E355", {"start": v(-1, 4.14) * mm, "end": v(-0.6, 3.67) * mm});
            skLineSegment(sketch, "E356", {"start": v(-0.6, 3.67) * mm, "end": v(-0.6, 3.3) * mm});
            skLineSegment(sketch, "E357", {"start": v(-0.6, 3.3) * mm, "end": v(-0.75, 2.92) * mm});
            skCircle(sketch, "E358", {"center": v(-1.88, 2.05) * mm, "radius": 0.36 * mm});
            skCircle(sketch, "E359", {"center": v(2, 1.98) * mm, "radius": 0.55 * mm});
            skLineSegment(sketch, "E360", {"start": v(1.28, 2.75) * mm, "end": v(1.2, 3.51) * mm});
            skLineSegment(sketch, "E361", {"start": v(1.2, 3.51) * mm, "end": v(1.48, 4.3) * mm});
            skLineSegment(sketch, "E362", {"start": v(1.48, 4.3) * mm, "end": v(1.97, 4.79) * mm});
            skLineSegment(sketch, "E363", {"start": v(1.97, 4.79) * mm, "end": v(2.61, 4.97) * mm});
            skLineSegment(sketch, "E364", {"start": v(2.61, 4.97) * mm, "end": v(3.48, 5) * mm});
            skLineSegment(sketch, "E365", {"start": v(3.48, 5) * mm, "end": v(3.84, 4.9) * mm});
            skLineSegment(sketch, "E366", {"start": v(3.84, 4.9) * mm, "end": v(4.24, 4.39) * mm});
            skLineSegment(sketch, "E367", {"start": v(4.24, 4.39) * mm, "end": v(4.62, 3.65) * mm});
            skLineSegment(sketch, "E368", {"start": v(4.62, 3.65) * mm, "end": v(5, 2.63) * mm});
            skLineSegment(sketch, "E369", {"start": v(5, 2.63) * mm, "end": v(5.05, 1.96) * mm});
            skLineSegment(sketch, "E370", {"start": v(5.05, 1.96) * mm, "end": v(4.95, 1.4) * mm});
            skLineSegment(sketch, "E371", {"start": v(4.95, 1.4) * mm, "end": v(4.72, 0.68) * mm});
            skLineSegment(sketch, "E372", {"start": v(4.72, 0.68) * mm, "end": v(4.53, 0.36) * mm});
            skLineSegment(sketch, "E373", {"start": v(4.53, 0.36) * mm, "end": v(4.05, 0.04) * mm});
            skLineSegment(sketch, "E374", {"start": v(4.05, 0.04) * mm, "end": v(3.47, -0.03) * mm});
            skLineSegment(sketch, "E375", {"start": v(3.47, -0.03) * mm, "end": v(2.8, 0.23) * mm});
            skLineSegment(sketch, "E376", {"start": v(2.8, 0.23) * mm, "end": v(2.36, 0.52) * mm});
            skLineSegment(sketch, "E377", {"start": v(2.36, 0.52) * mm, "end": v(2.1, 0.8) * mm});
            skLineSegment(sketch, "E378", {"start": v(2.1, 0.8) * mm, "end": v(2.75, 0.8) * mm});
            skLineSegment(sketch, "E379", {"start": v(2.75, 0.8) * mm, "end": v(3.16, 0.9) * mm});
            skLineSegment(sketch, "E380", {"start": v(3.16, 0.9) * mm, "end": v(3.46, 1.33) * mm});
            skLineSegment(sketch, "E381", {"start": v(3.46, 1.33) * mm, "end": v(3.65, 1.95) * mm});
            skLineSegment(sketch, "E382", {"start": v(3.65, 1.95) * mm, "end": v(3.47, 2.6) * mm});
            skLineSegment(sketch, "E383", {"start": v(3.47, 2.6) * mm, "end": v(2.94, 2.95) * mm});
            skLineSegment(sketch, "E384", {"start": v(2.94, 2.95) * mm, "end": v(2.28, 2.95) * mm});
            skLineSegment(sketch, "E385", {"start": v(2.28, 2.95) * mm, "end": v(1.7, 2.87) * mm});
            skLineSegment(sketch, "E386", {"start": v(1.7, 2.87) * mm, "end": v(1.28, 2.75) * mm});
            skLineSegment(sketch, "E387", {"start": v(1, 2.37) * mm, "end": v(0.9, 2.81) * mm});
            skLineSegment(sketch, "E388", {"start": v(0.9, 2.81) * mm, "end": v(0.85, 3.36) * mm});
            skLineSegment(sketch, "E389", {"start": v(0.85, 3.36) * mm, "end": v(1.03, 4.05) * mm});
            skLineSegment(sketch, "E390", {"start": v(1.03, 4.05) * mm, "end": v(1.38, 4.64) * mm});
            skLineSegment(sketch, "E391", {"start": v(1.38, 4.64) * mm, "end": v(1.93, 5.08) * mm});
            skLineSegment(sketch, "E392", {"start": v(1.93, 5.08) * mm, "end": v(2.65, 5.27) * mm});
            skLineSegment(sketch, "E393", {"start": v(2.65, 5.27) * mm, "end": v(3.25, 5.32) * mm});
            skLineSegment(sketch, "E394", {"start": v(3.25, 5.32) * mm, "end": v(3.74, 5.27) * mm});
            skLineSegment(sketch, "E395", {"start": v(3.74, 5.27) * mm, "end": v(4.25, 5.05) * mm});
            skLineSegment(sketch, "E396", {"start": v(4.25, 5.05) * mm, "end": v(4.61, 4.69) * mm});
            skLineSegment(sketch, "E397", {"start": v(4.61, 4.69) * mm, "end": v(4.89, 4.15) * mm});
            skLineSegment(sketch, "E398", {"start": v(4.89, 4.15) * mm, "end": v(5.3, 3.4) * mm});
            skLineSegment(sketch, "E399", {"start": v(5.3, 3.4) * mm, "end": v(5.5, 2.73) * mm});
            skLineSegment(sketch, "E400", {"start": v(5.5, 2.73) * mm, "end": v(5.45, 2.2) * mm});
            skLineSegment(sketch, "E401", {"start": v(5.45, 2.2) * mm, "end": v(5.27, 1.6) * mm});
            skLineSegment(sketch, "E402", {"start": v(5.27, 1.6) * mm, "end": v(5.13, 0.94) * mm});
            skLineSegment(sketch, "E403", {"start": v(5.13, 0.94) * mm, "end": v(4.89, 0.33) * mm});
            skLineSegment(sketch, "E404", {"start": v(4.89, 0.33) * mm, "end": v(4.32, -0.11) * mm});
            skLineSegment(sketch, "E405", {"start": v(4.32, -0.11) * mm, "end": v(3.96, -0.3) * mm});
            skLineSegment(sketch, "E406", {"start": v(3.96, -0.3) * mm, "end": v(3.4, -0.4) * mm});
            skLineSegment(sketch, "E407", {"start": v(3.4, -0.4) * mm, "end": v(2.86, -0.19) * mm});
            skLineSegment(sketch, "E408", {"start": v(2.86, -0.19) * mm, "end": v(2.17, 0.23) * mm});
            skLineSegment(sketch, "E409", {"start": v(2.17, 0.23) * mm, "end": v(1.64, 0.81) * mm});
            skLineSegment(sketch, "E410", {"start": v(1.64, 0.81) * mm, "end": v(1.37, 1.1) * mm});
            skLineSegment(sketch, "E411", {"start": v(1.37, 1.1) * mm, "end": v(0.95, 1.44) * mm});
            skLineSegment(sketch, "E412", {"start": v(0.95, 1.44) * mm, "end": v(0.88, 1.9) * mm});
            skLineSegment(sketch, "E413", {"start": v(0.88, 1.9) * mm, "end": v(1, 2.37) * mm});
            skLineSegment(sketch, "E414", {"start": v(9.4, 1.83) * mm, "end": v(9.07, 1.63) * mm});
            skLineSegment(sketch, "E415", {"start": v(9.07, 1.63) * mm, "end": v(8.87, 1.45) * mm});
            skLineSegment(sketch, "E416", {"start": v(8.87, 1.45) * mm, "end": v(9.03, 1.33) * mm});
            skLineSegment(sketch, "E417", {"start": v(9.03, 1.33) * mm, "end": v(9.47, 1.28) * mm});
            skLineSegment(sketch, "E418", {"start": v(9.47, 1.28) * mm, "end": v(10.04, 1.37) * mm});
            skLineSegment(sketch, "E419", {"start": v(10.04, 1.37) * mm, "end": v(10.34, 1.43) * mm});
            skLineSegment(sketch, "E420", {"start": v(10.34, 1.43) * mm, "end": v(10.26, 1.6) * mm});
            skLineSegment(sketch, "E421", {"start": v(10.26, 1.6) * mm, "end": v(10.02, 1.78) * mm});
            skLineSegment(sketch, "E422", {"start": v(10.02, 1.78) * mm, "end": v(9.6, 1.88) * mm});
            skLineSegment(sketch, "E423", {"start": v(9.6, 1.88) * mm, "end": v(9.4, 1.83) * mm});
            skLineSegment(sketch, "E424", {"start": v(-11.23, -4.07) * mm, "end": v(-10.12, -4.07) * mm});
            skSolve(sketch);
        }
        {
            var Q0;
            Q0=qSketchRegion(id+"F2",true);
            var Q1;
            Q1=makeQuery(id+"F2.imprint","IMPRINT",FACE,{"disambiguationData":[TD([[makeQuery(id+"F2.imprint","IMPRINT",EDGE,{"derivedFrom":sQuery(id+"F2.wireOp",EDGE,"E145")}),-1.0]])]});
            var Q2;
            Q2=makeQuery(id+"F2.imprint","IMPRINT",FACE,{"disambiguationData":[TD([[makeQuery(id+"F2.imprint","IMPRINT",EDGE,{"derivedFrom":sQuery(id+"F2.wireOp",EDGE,"E311")}),1.0]])]});
            var Q3;
            Q3=makeQuery(id+"F2.imprint","IMPRINT",FACE,{"disambiguationData":[TD([[makeQuery(id+"F2.imprint","IMPRINT",EDGE,{"derivedFrom":sQuery(id+"F2.wireOp",EDGE,"E359")}),-1.0]])]});
            extrude(context, id + "F3", {"entities" : qUnion([Q0, Q1, Q2, Q3]), "operationType" : NewBodyOperationType.ADD, "oppositeDirection" : true, "depth" : 3 * mm});
        }
        {
            var Q0;
            {var subQ0=sQuery(id+"F0.wireOp",EDGE,"E0.left");var subQ1=sQuery(id+"F0.wireOp",EDGE,"E0.bottom");var subQ2=sQuery(id+"F0.wireOp",EDGE,"E0.right");var subQ3=sQuery(id+"F0.wireOp",EDGE,"E0.top");Q0=makeQuery(id+"F3.boolean.opBoolean","SPLIT",FACE,{"disambiguationData":[TD([makeQuery(id+"F1.opExtrude","SWEPT_FACE",FACE,{"disambiguationData":[OSD([subQ1])]})])],"derivedFrom":makeQuery(id+"F1.opExtrude","CAP_FACE",FACE,{"disambiguationData":[OSD([subQ1,subQ3,subQ0,subQ2])],"isStart":true})});}
            var sketch = newSketch(context, id + "F4", { "sketchPlane" : qUnion([Q0])});
            skCircle(sketch, "E425", {"center": v(0, 0) * mm, "radius": 21.5 * mm});
            skSolve(sketch);
        }
        {
            var Q0;
            Q0=makeQuery(id+"F4.imprint","IMPRINT",FACE,{"disambiguationData":[TD([[makeQuery(id+"F4.imprint","IMPRINT",EDGE,{"derivedFrom":sQuery(id+"F4.wireOp",EDGE,"E425")}),-1.0]])]});
            extrude(context, id + "F5", {"entities" : qUnion([Q0]), "operationType" : NewBodyOperationType.REMOVE, "endBound" : BoundingType.THROUGH_ALL, "oppositeDirection" : true, "depth" : 25 * mm});
        }
    });
